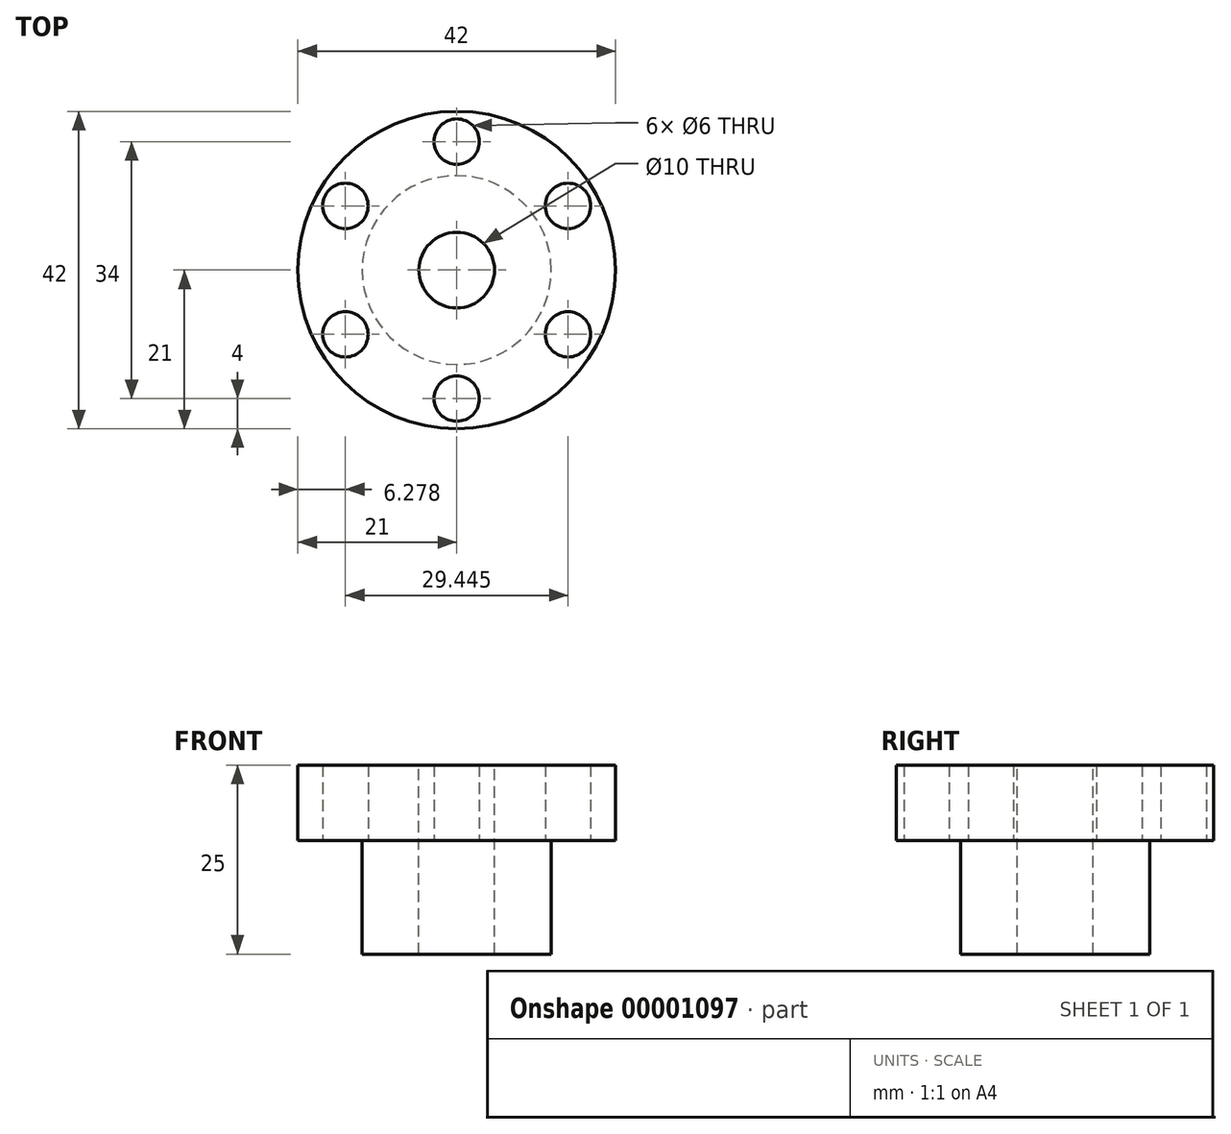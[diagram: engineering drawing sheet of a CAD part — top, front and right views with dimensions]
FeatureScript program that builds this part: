
annotation { "Feature Type Name" : "Feature", "Feature Type Description" : "" }
export const myFeature = defineFeature(function(context is Context, id is Id, definition is map)
    precondition{}
    {
        {
            var Q0;
            Q0=qCreatedBy(makeId("Front.planeOp"),FACE);
            var sketch = newSketch(context, id + "F0", { "sketchPlane" : qUnion([Q0])});
            skLineSegment(sketch, "E0", {"start": v(21, 0) * mm, "end": v(21, -10) * mm});
            skLineSegment(sketch, "E1", {"start": v(21, -10) * mm, "end": v(12.5, -10) * mm});
            skLineSegment(sketch, "E2", {"start": v(12.5, -10) * mm, "end": v(12.5, -25) * mm});
            skLineSegment(sketch, "E3", {"start": v(21, 0) * mm, "end": v(5, 0) * mm});
            skLineSegment(sketch, "E4", {"start": v(5, 0) * mm, "end": v(5, -25) * mm});
            skLineSegment(sketch, "E5", {"start": v(5, -25) * mm, "end": v(12.5, -25) * mm});
            skLineSegment(sketch, "E6", {"start": v(0, 36.15) * mm, "end": v(0, -62.44) * mm, "construction": true});
            skSolve(sketch);
        }
        {
            var Q0;
            Q0 = qSketchRegion(id + "F0", true);
            var Q1;
            Q1=sQuery(id+"F0.wireOp",EDGE,"E6");
            revolve(context, id + "F1", {"entities" : qUnion([Q0]), "axis" : qUnion([Q1]), "revolveType" : RevolveType.FULL});
        }
        {
            var Q0;
            Q0=qCreatedBy(makeId("Top.planeOp"),FACE);
            var sketch = newSketch(context, id + "F2", { "sketchPlane" : qUnion([Q0])});
            skCircle(sketch, "E7.cCircle", {"center": v(0, 0) * mm, "radius": 14.72 * mm, "construction": true});
            skLineSegment(sketch, "E7.0", {"start": v(-14.72, 8.5) * mm, "end": v(0, 17) * mm, "construction": true});
            skLineSegment(sketch, "E7.1", {"start": v(0, 17) * mm, "end": v(14.72, 8.5) * mm, "construction": true});
            skLineSegment(sketch, "E7.2", {"start": v(14.72, 8.5) * mm, "end": v(14.72, -8.5) * mm, "construction": true});
            skLineSegment(sketch, "E7.3", {"start": v(14.72, -8.5) * mm, "end": v(0, -17) * mm, "construction": true});
            skLineSegment(sketch, "E7.4", {"start": v(0, -17) * mm, "end": v(-14.72, -8.5) * mm, "construction": true});
            skLineSegment(sketch, "E7.5", {"start": v(-14.72, -8.5) * mm, "end": v(-14.72, 8.5) * mm, "construction": true});
            skPoint(sketch, "E7.0.midPoint", {"position": v(-7.36, 12.75) * mm});
            skCircle(sketch, "E8", {"center": v(0, 0) * mm, "radius": 17 * mm, "construction": true});
            skSolve(sketch);
        }
        {
            var Q0;
            Q0=sQuery(id+"F2.wireOp",VERTEX,"E7.5.start");
            var Q1;
            Q1=sQuery(id+"F2.wireOp",VERTEX,"E7.0.start");
            var Q2;
            Q2=sQuery(id+"F2.wireOp",VERTEX,"E7.1.start");
            var Q3;
            Q3=sQuery(id+"F2.wireOp",VERTEX,"E7.2.start");
            var Q4;
            Q4=sQuery(id+"F2.wireOp",VERTEX,"E7.3.start");
            var Q5;
            Q5=sQuery(id+"F2.wireOp",VERTEX,"E7.4.start");
            var Q6;
            Q6=makeQuery(id+"F1.opRevolve","SWEPT_BODY",BODY,{"disambiguationData":[OSD([sQuery(id+"F0.wireOp",EDGE,"E0"),sQuery(id+"F0.wireOp",EDGE,"E1"),sQuery(id+"F0.wireOp",EDGE,"E2"),sQuery(id+"F0.wireOp",EDGE,"E3"),sQuery(id+"F0.wireOp",EDGE,"E4"),sQuery(id+"F0.wireOp",EDGE,"E5")])]});
            hole(context, id + "F3", {"style" : HoleStyle.SIMPLE, "endStyle" : HoleEndStyle.THROUGH, "holeDiameter" : 6 * mm, "locations" : qUnion([Q0, Q1, Q2, Q3, Q4, Q5]), "scope" : qUnion([Q6]), "isTappedThrough" : true});
        }
    });
